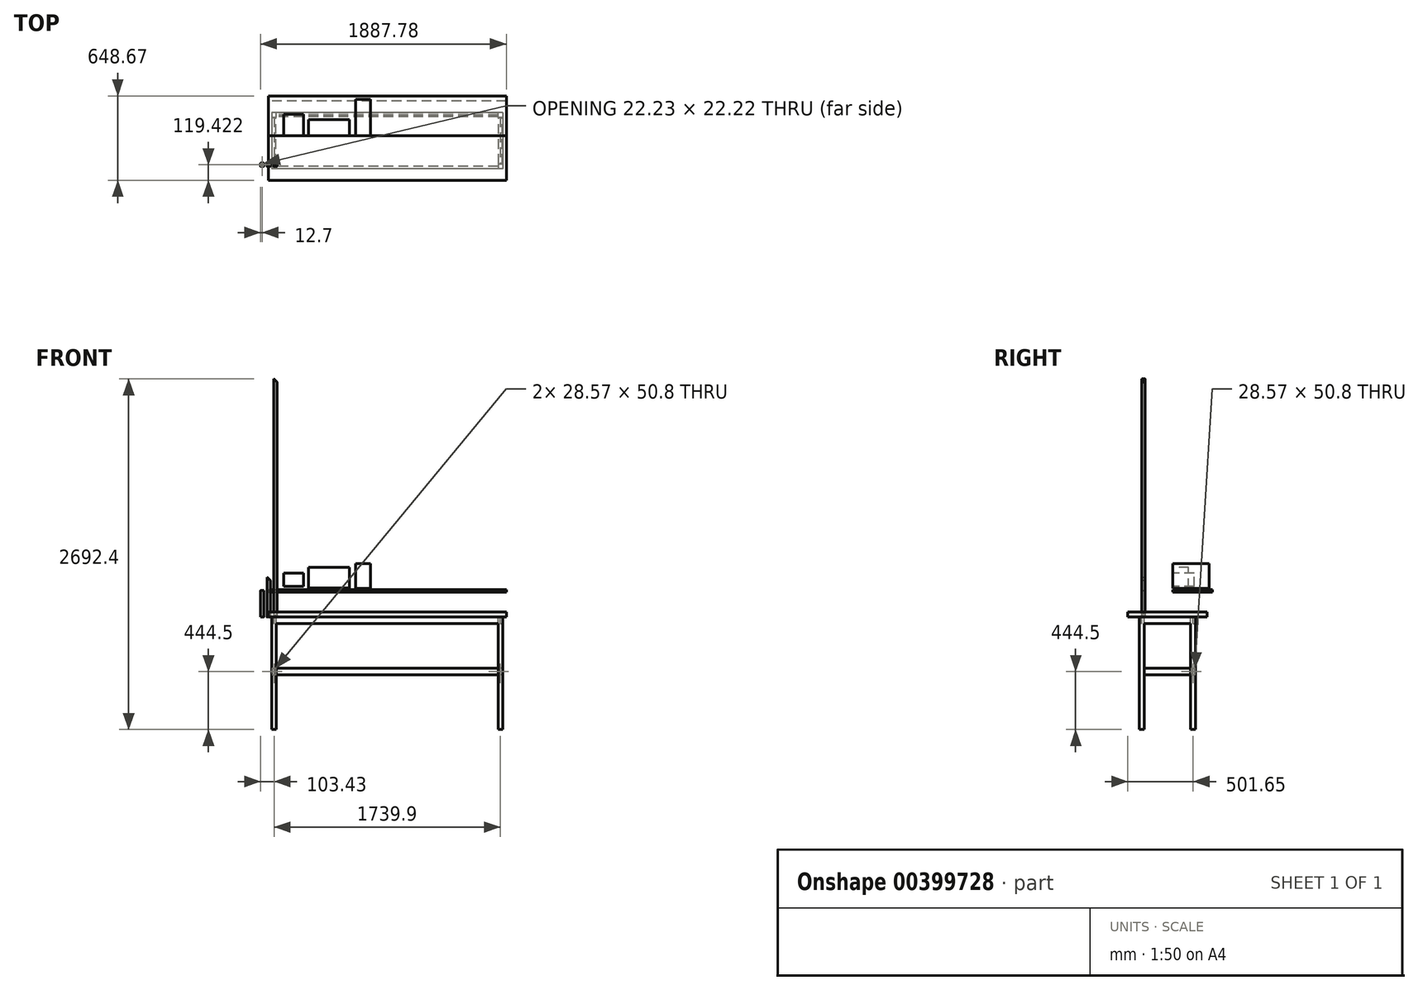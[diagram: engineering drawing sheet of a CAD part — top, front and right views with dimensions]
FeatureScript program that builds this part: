
annotation { "Feature Type Name" : "Feature", "Feature Type Description" : "" }
export const myFeature = defineFeature(function(context is Context, id is Id, definition is map)
    precondition{}
    {
        {
            var Q0;
            Q0=qCreatedBy(makeId("Top.planeOp"),FACE);
            var sketch = newSketch(context, id + "F0", { "sketchPlane" : qUnion([Q0])});
            skLineSegment(sketch, "E0.bottom", {"start": v(914.4, -304.8) * mm, "end": v(-914.4, -304.8) * mm});
            skLineSegment(sketch, "E0.top", {"start": v(914.4, 304.8) * mm, "end": v(-914.4, 304.8) * mm});
            skLineSegment(sketch, "E0.left", {"start": v(914.4, -304.8) * mm, "end": v(914.4, 304.8) * mm});
            skLineSegment(sketch, "E0.right", {"start": v(-914.4, -304.8) * mm, "end": v(-914.4, 304.8) * mm});
            skPoint(sketch, "E0.middle", {"position": v(0, 0) * mm});
            skSolve(sketch);
        }
        {
            var Q0;
            Q0=makeQuery(id+"F0.imprint","IMPRINT",FACE,{"disambiguationData":[TD([[makeQuery(id+"F0.imprint","IMPRINT",EDGE,{"derivedFrom":sQuery(id+"F0.wireOp",EDGE,"E0.bottom")}),-1.0]])]});
            extrude(context, id + "F1", {"entities" : qUnion([Q0]), "depth" : 38.1 * mm});
        }
        {
            var Q0;
            Q0=makeQuery(id+"F0.imprint","IMPRINT",FACE,{"disambiguationData":[TD([[makeQuery(id+"F0.imprint","IMPRINT",EDGE,{"derivedFrom":sQuery(id+"F0.wireOp",EDGE,"E0.bottom")}),-1.0]])]});
            var sketch = newSketch(context, id + "F2", { "sketchPlane" : qUnion([Q0])});
            skLineSegment(sketch, "E1.bottom", {"start": v(889, 215.9) * mm, "end": v(-889, 215.9) * mm});
            skLineSegment(sketch, "E1.top", {"start": v(889, -215.9) * mm, "end": v(-889, -215.9) * mm});
            skLineSegment(sketch, "E1.left", {"start": v(889, 215.9) * mm, "end": v(889, -215.9) * mm});
            skLineSegment(sketch, "E1.right", {"start": v(-889, 215.9) * mm, "end": v(-889, -215.9) * mm});
            skPoint(sketch, "E1.middle", {"position": v(0, 0) * mm});
            skLineSegment(sketch, "E2.bottom", {"start": v(850.9, 196.85) * mm, "end": v(-850.9, 196.85) * mm});
            skLineSegment(sketch, "E2.top", {"start": v(850.9, -196.85) * mm, "end": v(-850.9, -196.85) * mm});
            skLineSegment(sketch, "E2.left", {"start": v(869.95, 177.8) * mm, "end": v(869.95, -177.8) * mm});
            skLineSegment(sketch, "E2.right", {"start": v(-869.95, 177.8) * mm, "end": v(-869.95, -177.8) * mm});
            skLineSegment(sketch, "E3", {"start": v(0, -215.9) * mm, "end": v(0, 215.9) * mm, "construction": true});
            skPoint(sketch, "E4", {"position": v(-850.9, -177.8) * mm});
            skLineSegment(sketch, "E5", {"start": v(-889, 0) * mm, "end": v(0, 0) * mm, "construction": true});
            skLineSegment(sketch, "E6", {"start": v(-850.9, -177.8) * mm, "end": v(-889, -177.8) * mm});
            skLineSegment(sketch, "E7", {"start": v(-850.9, -177.8) * mm, "end": v(-850.9, -215.9) * mm});
            skLineSegment(sketch, "E8.MirrorCS", {"start": v(-850.9, 177.8) * mm, "end": v(-889, 177.8) * mm});
            skLineSegment(sketch, "E9.MirrorCS", {"start": v(-850.9, 177.8) * mm, "end": v(-850.9, 215.9) * mm});
            skLineSegment(sketch, "E10.MirrorCS", {"start": v(850.9, -177.8) * mm, "end": v(850.9, -215.9) * mm});
            skLineSegment(sketch, "E11.MirrorCS", {"start": v(850.9, -177.8) * mm, "end": v(889, -177.8) * mm});
            skLineSegment(sketch, "E12.MirrorCS", {"start": v(850.9, 177.8) * mm, "end": v(889, 177.8) * mm});
            skLineSegment(sketch, "E13.MirrorCS", {"start": v(850.9, 177.8) * mm, "end": v(850.9, 215.9) * mm});
            skPoint(sketch, "E14.orphan", {"position": v(869.95, -196.85) * mm});
            skPoint(sketch, "E15.orphan", {"position": v(869.95, 196.85) * mm});
            skPoint(sketch, "E16.orphan", {"position": v(-869.95, -196.85) * mm});
            skPoint(sketch, "E17.orphan", {"position": v(-869.95, 196.85) * mm});
            skSolve(sketch);
        }
        {
            var Q0;
            {var subQ0=sQuery(id+"F2.wireOp",EDGE,"E9.MirrorCS");var subQ1=sQuery(id+"F2.wireOp",EDGE,"E1.bottom");var subQ2=makeQuery(id+"F2.imprint","INTERSECT",VERTEX,{"derivedFrom":[subQ1,subQ0]});Q0=makeQuery(id+"F2.imprint","IMPRINT",FACE,{"disambiguationData":[TD([[makeQuery(id+"F2.imprint","IMPRINT",EDGE,{"disambiguationData":[TD([[subQ2,1.0]])],"derivedFrom":subQ1}),1.0]])]});}
            var Q1;
            {var subQ0=sQuery(id+"F2.wireOp",EDGE,"E7");var subQ1=sQuery(id+"F2.wireOp",EDGE,"E1.top");var subQ2=makeQuery(id+"F2.imprint","INTERSECT",VERTEX,{"derivedFrom":[subQ1,subQ0]});Q1=makeQuery(id+"F2.imprint","IMPRINT",FACE,{"disambiguationData":[TD([[makeQuery(id+"F2.imprint","IMPRINT",EDGE,{"disambiguationData":[TD([[subQ2,1.0]])],"derivedFrom":subQ1}),-1.0]])]});}
            var Q2;
            {var subQ0=sQuery(id+"F2.wireOp",EDGE,"E11.MirrorCS");var subQ1=sQuery(id+"F2.wireOp",EDGE,"E1.left");var subQ2=makeQuery(id+"F2.imprint","INTERSECT",VERTEX,{"derivedFrom":[subQ1,subQ0]});Q2=makeQuery(id+"F2.imprint","IMPRINT",FACE,{"disambiguationData":[TD([[makeQuery(id+"F2.imprint","IMPRINT",EDGE,{"disambiguationData":[TD([[subQ2,1.0]])],"derivedFrom":subQ1}),-1.0]])]});}
            var Q3;
            {var subQ0=sQuery(id+"F2.wireOp",EDGE,"E6");var subQ1=sQuery(id+"F2.wireOp",EDGE,"E1.right");var subQ2=makeQuery(id+"F2.imprint","INTERSECT",VERTEX,{"derivedFrom":[subQ1,subQ0]});Q3=makeQuery(id+"F2.imprint","IMPRINT",FACE,{"disambiguationData":[TD([[makeQuery(id+"F2.imprint","IMPRINT",EDGE,{"disambiguationData":[TD([[subQ2,1.0]])],"derivedFrom":subQ1}),1.0]])]});}
            extrude(context, id + "F3", {"entities" : qUnion([Q0, Q1, Q2, Q3]), "oppositeDirection" : true, "depth" : 50.8 * mm});
        }
        {
            var Q0;
            {var subQ2=sQuery(id+"F2.wireOp",EDGE,"E1.right");var subQ6=sQuery(id+"F2.wireOp",EDGE,"E1.top");var subQ7=makeQuery(id+"F2.imprint","INTERSECT",VERTEX,{"derivedFrom":[subQ6,subQ2]});Q0=makeQuery(id+"F2.imprint","IMPRINT",FACE,{"disambiguationData":[TD([[makeQuery(id+"F2.imprint","IMPRINT",EDGE,{"disambiguationData":[TD([[subQ7,1.0]])],"derivedFrom":subQ6}),-1.0]])]});}
            var Q1;
            {var subQ2=sQuery(id+"F2.wireOp",EDGE,"E1.right");var subQ6=sQuery(id+"F2.wireOp",EDGE,"E1.bottom");var subQ7=makeQuery(id+"F2.imprint","INTERSECT",VERTEX,{"derivedFrom":[subQ6,subQ2]});Q1=makeQuery(id+"F2.imprint","IMPRINT",FACE,{"disambiguationData":[TD([[makeQuery(id+"F2.imprint","IMPRINT",EDGE,{"disambiguationData":[TD([[subQ7,1.0]])],"derivedFrom":subQ6}),1.0]])]});}
            var Q2;
            {var subQ2=sQuery(id+"F2.wireOp",EDGE,"E1.top");var subQ4=sQuery(id+"F2.wireOp",EDGE,"E1.left");var subQ5=makeQuery(id+"F2.imprint","INTERSECT",VERTEX,{"derivedFrom":[subQ2,subQ4]});Q2=makeQuery(id+"F2.imprint","IMPRINT",FACE,{"disambiguationData":[TD([[makeQuery(id+"F2.imprint","IMPRINT",EDGE,{"disambiguationData":[TD([[subQ5,-1.0]])],"derivedFrom":subQ2}),-1.0]])]});}
            var Q3;
            {var subQ2=sQuery(id+"F2.wireOp",EDGE,"E1.left");var subQ6=sQuery(id+"F2.wireOp",EDGE,"E1.bottom");var subQ7=makeQuery(id+"F2.imprint","INTERSECT",VERTEX,{"derivedFrom":[subQ6,subQ2]});Q3=makeQuery(id+"F2.imprint","IMPRINT",FACE,{"disambiguationData":[TD([[makeQuery(id+"F2.imprint","IMPRINT",EDGE,{"disambiguationData":[TD([[subQ7,-1.0]])],"derivedFrom":subQ6}),1.0]])]});}
            extrude(context, id + "F4", {"entities" : qUnion([Q0, Q1, Q2, Q3]), "operationType" : NewBodyOperationType.ADD, "oppositeDirection" : true, "depth" : 863.6 * mm});
        }
        {
            var Q0;
            Q0=makeQuery(id+"F4.opExtrude","SWEPT_FACE",FACE,{"disambiguationData":[OSD([sQuery(id+"F2.wireOp",EDGE,"E9.MirrorCS")])]});
            var sketch = newSketch(context, id + "F5", { "sketchPlane" : qUnion([Q0])});
            skLineSegment(sketch, "E18", {"start": v(182.56, -393.7) * mm, "end": v(211.14, -393.7) * mm});
            skLineSegment(sketch, "E19", {"start": v(182.56, -444.5) * mm, "end": v(211.14, -444.5) * mm});
            skLineSegment(sketch, "E20", {"start": v(211.14, -393.7) * mm, "end": v(211.14, -444.5) * mm});
            skLineSegment(sketch, "E21", {"start": v(182.56, -393.7) * mm, "end": v(182.56, -444.5) * mm});
            skPoint(sketch, "E22", {"position": v(196.85, -393.7) * mm});
            skPoint(sketch, "E23", {"position": v(182.56, -419.1) * mm});
            skPoint(sketch, "E24", {"position": v(211.14, -419.1) * mm});
            skLineSegment(sketch, "E25", {"start": v(177.8, -385.16) * mm, "end": v(215.9, -385.16) * mm, "construction": true});
            skLineSegment(sketch, "E26", {"start": v(196.85, -385.16) * mm, "end": v(196.85, -459.18) * mm, "construction": true});
            skSolve(sketch);
        }
        {
            var Q0;
            Q0=makeQuery(id+"F5.imprint","IMPRINT",FACE,{"disambiguationData":[TD([[makeQuery(id+"F5.imprint","IMPRINT",EDGE,{"derivedFrom":sQuery(id+"F5.wireOp",EDGE,"E18")}),-1.0]])]});
            extrude(context, id + "F6", {"entities" : qUnion([Q0]), "operationType" : NewBodyOperationType.ADD, "endBound" : BoundingType.UP_TO_NEXT, "depth" : 25.4 * mm});
        }
        {
            var Q0;
            Q0=makeQuery(id+"F4.opExtrude","SWEPT_FACE",FACE,{"disambiguationData":[OSD([sQuery(id+"F2.wireOp",EDGE,"E8.MirrorCS")])]});
            var sketch = newSketch(context, id + "F7", { "sketchPlane" : qUnion([Q0])});
            skLineSegment(sketch, "E27", {"start": v(-884.24, -393.7) * mm, "end": v(-855.66, -393.7) * mm});
            skLineSegment(sketch, "E28", {"start": v(-884.24, -444.5) * mm, "end": v(-855.66, -444.5) * mm});
            skLineSegment(sketch, "E29", {"start": v(-855.66, -393.7) * mm, "end": v(-855.66, -444.5) * mm});
            skLineSegment(sketch, "E30", {"start": v(-884.24, -393.7) * mm, "end": v(-884.24, -444.5) * mm});
            skLineSegment(sketch, "E31", {"start": v(-889, -376.97) * mm, "end": v(-850.9, -376.97) * mm, "construction": true});
            skLineSegment(sketch, "E32", {"start": v(-869.95, -376.97) * mm, "end": v(-869.95, -445.4) * mm, "construction": true});
            skPoint(sketch, "E33", {"position": v(-884.24, -419.1) * mm});
            skPoint(sketch, "E34", {"position": v(-855.66, -419.1) * mm});
            skSolve(sketch);
        }
        {
            var Q0;
            Q0=makeQuery(id+"F7.imprint","IMPRINT",FACE,{"disambiguationData":[TD([[makeQuery(id+"F7.imprint","IMPRINT",EDGE,{"derivedFrom":sQuery(id+"F7.wireOp",EDGE,"E27")}),-1.0]])]});
            extrude(context, id + "F8", {"entities" : qUnion([Q0]), "endBound" : BoundingType.UP_TO_NEXT, "depth" : 25.4 * mm});
        }
        {
            var Q0;
            Q0=makeQuery(id+"F8.opExtrude","SWEPT_BODY",BODY,{"disambiguationData":[OSD([sQuery(id+"F7.wireOp",EDGE,"E27"),sQuery(id+"F7.wireOp",EDGE,"E28"),sQuery(id+"F7.wireOp",EDGE,"E29"),sQuery(id+"F7.wireOp",EDGE,"E30")])]});
            var Q1;
            Q1=qCreatedBy(makeId("Right.planeOp"),FACE);
            mirror(context, id + "F9", {"operationType" : NewBodyOperationType.ADD, "entities" : qUnion([Q0]), "mirrorPlane" : qUnion([Q1])});
        }
        {
            var Q0;
            Q0=makeQuery(id+"F1.opExtrude","CAP_FACE",FACE,{"disambiguationData":[OSD([sQuery(id+"F0.wireOp",EDGE,"E0.bottom"),sQuery(id+"F0.wireOp",EDGE,"E0.top"),sQuery(id+"F0.wireOp",EDGE,"E0.left"),sQuery(id+"F0.wireOp",EDGE,"E0.right")])],"isStart":false});
            cPlane(context, id + "F10", {"entities" : qUnion([Q0]), "cplaneType" : CPlaneType.OFFSET, "offset" : 152.4 * mm, "width" : 152.4 * mm, "height" : 152.4 * mm});
        }
        {
            var Q0;
            Q0=qCreatedBy(id+"F10.planeOp",FACE);
            var sketch = newSketch(context, id + "F11", { "sketchPlane" : qUnion([Q0])});
            skLineSegment(sketch, "E35.bottom", {"start": v(-914.4, 343.87) * mm, "end": v(914.4, 343.87) * mm});
            skLineSegment(sketch, "E35.top", {"start": v(-914.4, 39.07) * mm, "end": v(914.4, 39.07) * mm});
            skLineSegment(sketch, "E35.left", {"start": v(-914.4, 343.87) * mm, "end": v(-914.4, 39.07) * mm});
            skLineSegment(sketch, "E35.right", {"start": v(914.4, 343.87) * mm, "end": v(914.4, 39.07) * mm});
            skLineSegment(sketch, "E36", {"start": v(0, 343.87) * mm, "end": v(0, 39.07) * mm, "construction": true});
            skLineSegment(sketch, "E37", {"start": v(0, -304.8) * mm, "end": v(0, 304.8) * mm, "construction": true});
            skSolve(sketch);
        }
        {
            var Q0;
            Q0=makeQuery(id+"F11.imprint","IMPRINT",FACE,{"disambiguationData":[TD([[makeQuery(id+"F11.imprint","IMPRINT",EDGE,{"derivedFrom":sQuery(id+"F11.wireOp",EDGE,"E35.bottom")}),-1.0]])]});
            extrude(context, id + "F12", {"entities" : qUnion([Q0]), "depth" : 19.05 * mm});
        }
        {
            var Q0;
            Q0=makeQuery(id+"F12.opExtrude","SWEPT_FACE",FACE,{"disambiguationData":[OSD([sQuery(id+"F11.wireOp",EDGE,"E35.top")])]});
            var sketch = newSketch(context, id + "F13", { "sketchPlane" : qUnion([Q0])});
            skLineSegment(sketch, "E38.bottom", {"start": v(-796.5, 234.27) * mm, "end": v(-644.1, 234.27) * mm});
            skLineSegment(sketch, "E38.top", {"start": v(-796.5, 335.87) * mm, "end": v(-644.1, 335.87) * mm});
            skLineSegment(sketch, "E38.left", {"start": v(-796.5, 234.27) * mm, "end": v(-796.5, 335.87) * mm});
            skLineSegment(sketch, "E38.right", {"start": v(-644.1, 234.27) * mm, "end": v(-644.1, 335.87) * mm});
            skSolve(sketch);
        }
        {
            var Q0;
            Q0=makeQuery(id+"F13.imprint","IMPRINT",FACE,{"disambiguationData":[TD([[makeQuery(id+"F13.imprint","IMPRINT",EDGE,{"derivedFrom":sQuery(id+"F13.wireOp",EDGE,"E38.bottom")}),1.0]])]});
            extrude(context, id + "F14", {"entities" : qUnion([Q0]), "oppositeDirection" : true, "depth" : 165.1 * mm});
        }
        {
            var Q0;
            Q0=makeQuery(id+"F12.opExtrude","SWEPT_FACE",FACE,{"disambiguationData":[OSD([sQuery(id+"F11.wireOp",EDGE,"E35.top")])]});
            var sketch = newSketch(context, id + "F15", { "sketchPlane" : qUnion([Q0])});
            skLineSegment(sketch, "E39.bottom", {"start": v(-604.6, 221.37) * mm, "end": v(-291.5, 221.37) * mm});
            skLineSegment(sketch, "E39.top", {"start": v(-604.6, 382.17) * mm, "end": v(-291.5, 382.17) * mm});
            skLineSegment(sketch, "E39.left", {"start": v(-604.6, 221.37) * mm, "end": v(-604.6, 382.17) * mm});
            skLineSegment(sketch, "E39.right", {"start": v(-291.5, 221.37) * mm, "end": v(-291.5, 382.17) * mm});
            skSolve(sketch);
        }
        {
            var Q0;
            Q0=makeQuery(id+"F15.imprint","IMPRINT",FACE,{"disambiguationData":[TD([[makeQuery(id+"F15.imprint","IMPRINT",EDGE,{"derivedFrom":sQuery(id+"F15.wireOp",EDGE,"E39.bottom")}),1.0]])]});
            extrude(context, id + "F16", {"entities" : qUnion([Q0]), "oppositeDirection" : true, "depth" : 122.4 * mm});
        }
        {
            var Q0;
            Q0=makeQuery(id+"F12.opExtrude","SWEPT_FACE",FACE,{"disambiguationData":[OSD([sQuery(id+"F11.wireOp",EDGE,"E35.top")])]});
            var sketch = newSketch(context, id + "F17", { "sketchPlane" : qUnion([Q0])});
            skLineSegment(sketch, "E40.bottom", {"start": v(-243.83, 409.85) * mm, "end": v(-129.53, 409.85) * mm});
            skLineSegment(sketch, "E40.top", {"start": v(-243.83, 219.35) * mm, "end": v(-129.53, 219.35) * mm});
            skLineSegment(sketch, "E40.left", {"start": v(-243.83, 409.85) * mm, "end": v(-243.83, 219.35) * mm});
            skLineSegment(sketch, "E40.right", {"start": v(-129.53, 409.85) * mm, "end": v(-129.53, 219.35) * mm});
            skSolve(sketch);
        }
        {
            var Q0;
            Q0=makeQuery(id+"F17.imprint","IMPRINT",FACE,{"disambiguationData":[TD([[makeQuery(id+"F17.imprint","IMPRINT",EDGE,{"derivedFrom":sQuery(id+"F17.wireOp",EDGE,"E40.bottom")}),-1.0]])]});
            extrude(context, id + "F18", {"entities" : qUnion([Q0]), "oppositeDirection" : true, "depth" : 279.4 * mm});
        }
        {
            var Q0;
            Q0=makeQuery(id+"F12.opExtrude","CAP_FACE",FACE,{"disambiguationData":[OSD([sQuery(id+"F11.wireOp",EDGE,"E35.bottom"),sQuery(id+"F11.wireOp",EDGE,"E35.top"),sQuery(id+"F11.wireOp",EDGE,"E35.left"),sQuery(id+"F11.wireOp",EDGE,"E35.right")])],"isStart":true});
            var sketch = newSketch(context, id + "F19", { "sketchPlane" : qUnion([Q0])});
            skLineSegment(sketch, "E41.0", {"start": v(-914.4, -39.07) * mm, "end": v(914.4, -39.07) * mm});
            skLineSegment(sketch, "E42.0", {"start": v(-914.4, -343.87) * mm, "end": v(-914.4, -39.07) * mm});
            skLineSegment(sketch, "E43.0", {"start": v(-914.4, -343.87) * mm, "end": v(914.4, -343.87) * mm});
            skLineSegment(sketch, "E44.0", {"start": v(914.4, -343.87) * mm, "end": v(914.4, -39.07) * mm});
            skLineSegment(sketch, "E45", {"start": v(-914.4, -64.47) * mm, "end": v(914.4, -64.47) * mm});
            skLineSegment(sketch, "E46", {"start": v(-914.4, -318.47) * mm, "end": v(914.4, -318.47) * mm});
            skLineSegment(sketch, "E47", {"start": v(-889, -64.47) * mm, "end": v(-889, -318.47) * mm});
            skLineSegment(sketch, "E48", {"start": v(889, -64.47) * mm, "end": v(889, -318.47) * mm});
            skSolve(sketch);
        }
        {
            var Q0;
            Q0=qCreatedBy(makeId("Top.planeOp"),FACE);
            var sketch = newSketch(context, id + "F20", { "sketchPlane" : qUnion([Q0])});
            skLineSegment(sketch, "E49.bottom", {"start": v(-871.14, -198.08) * mm, "end": v(-847.01, -198.08) * mm});
            skLineSegment(sketch, "E49.top", {"start": v(-871.14, -172.68) * mm, "end": v(-847.01, -172.68) * mm});
            skLineSegment(sketch, "E49.left", {"start": v(-871.78, -197.44) * mm, "end": v(-871.78, -173.31) * mm});
            skLineSegment(sketch, "E49.right", {"start": v(-846.38, -197.44) * mm, "end": v(-846.38, -173.31) * mm});
            skLineSegment(sketch, "E50.0", {"start": v(-869.56, -196.5) * mm, "end": v(-848.6, -196.5) * mm});
            skLineSegment(sketch, "E50.1", {"start": v(-870.2, -195.86) * mm, "end": v(-870.2, -174.9) * mm});
            skLineSegment(sketch, "E50.2", {"start": v(-869.56, -174.27) * mm, "end": v(-848.6, -174.27) * mm});
            skLineSegment(sketch, "E50.3", {"start": v(-847.97, -195.86) * mm, "end": v(-847.97, -174.9) * mm});
            skPoint(sketch, "E51.visualSharp", {"position": v(-846.38, -198.08) * mm});
            skArc(sketch, "E51.filletArc", {"start": v(-847.01, -198.08) * mm, "mid": v(-846.57, -197.9) * mm, "end": v(-846.38, -197.44) * mm});
            skPoint(sketch, "E52.visualSharp", {"position": v(-846.38, -172.68) * mm});
            skArc(sketch, "E52.filletArc", {"start": v(-846.38, -173.31) * mm, "mid": v(-846.57, -172.86) * mm, "end": v(-847.01, -172.68) * mm});
            skPoint(sketch, "E53.visualSharp", {"position": v(-871.78, -172.68) * mm});
            skArc(sketch, "E53.filletArc", {"start": v(-871.14, -172.68) * mm, "mid": v(-871.6, -172.86) * mm, "end": v(-871.78, -173.31) * mm});
            skPoint(sketch, "E54.visualSharp", {"position": v(-871.78, -198.08) * mm});
            skArc(sketch, "E54.filletArc", {"start": v(-871.78, -197.44) * mm, "mid": v(-871.6, -197.9) * mm, "end": v(-871.14, -198.08) * mm});
            skPoint(sketch, "E55.visualSharp", {"position": v(-847.97, -196.5) * mm});
            skArc(sketch, "E55.filletArc", {"start": v(-848.6, -196.5) * mm, "mid": v(-848.15, -196.3) * mm, "end": v(-847.97, -195.86) * mm});
            skPoint(sketch, "E56.visualSharp", {"position": v(-847.97, -174.27) * mm});
            skArc(sketch, "E56.filletArc", {"start": v(-847.97, -174.9) * mm, "mid": v(-848.15, -174.45) * mm, "end": v(-848.6, -174.27) * mm});
            skPoint(sketch, "E57.visualSharp", {"position": v(-870.2, -174.27) * mm});
            skArc(sketch, "E57.filletArc", {"start": v(-869.56, -174.27) * mm, "mid": v(-870, -174.45) * mm, "end": v(-870.2, -174.9) * mm});
            skPoint(sketch, "E58.visualSharp", {"position": v(-870.2, -196.5) * mm});
            skArc(sketch, "E58.filletArc", {"start": v(-870.2, -195.86) * mm, "mid": v(-870, -196.3) * mm, "end": v(-869.56, -196.5) * mm});
            skLineSegment(sketch, "E59.1.0.0", {"start": v(-921.94, -198.08) * mm, "end": v(-897.81, -198.08) * mm});
            skArc(sketch, "E59.1.0.1", {"start": v(-922.58, -197.44) * mm, "mid": v(-922.4, -197.9) * mm, "end": v(-921.94, -198.08) * mm});
            skLineSegment(sketch, "E59.1.0.2", {"start": v(-922.58, -197.44) * mm, "end": v(-922.58, -173.31) * mm});
            skArc(sketch, "E59.1.0.3", {"start": v(-921.94, -172.68) * mm, "mid": v(-922.4, -172.86) * mm, "end": v(-922.58, -173.31) * mm});
            skLineSegment(sketch, "E59.1.0.4", {"start": v(-921.94, -172.68) * mm, "end": v(-897.81, -172.68) * mm});
            skArc(sketch, "E59.1.0.5", {"start": v(-897.18, -173.31) * mm, "mid": v(-897.37, -172.86) * mm, "end": v(-897.81, -172.68) * mm});
            skLineSegment(sketch, "E59.1.0.6", {"start": v(-897.18, -197.44) * mm, "end": v(-897.18, -173.31) * mm});
            skArc(sketch, "E59.1.0.7", {"start": v(-897.81, -198.08) * mm, "mid": v(-897.37, -197.9) * mm, "end": v(-897.18, -197.44) * mm});
            skArc(sketch, "E59.1.0.8", {"start": v(-899.4, -196.5) * mm, "mid": v(-898.95, -196.3) * mm, "end": v(-898.77, -195.86) * mm});
            skLineSegment(sketch, "E59.1.0.9", {"start": v(-898.77, -195.86) * mm, "end": v(-898.77, -174.9) * mm});
            skArc(sketch, "E59.1.0.10", {"start": v(-898.77, -174.9) * mm, "mid": v(-898.95, -174.45) * mm, "end": v(-899.4, -174.27) * mm});
            skLineSegment(sketch, "E59.1.0.11", {"start": v(-920.36, -174.27) * mm, "end": v(-899.4, -174.27) * mm});
            skArc(sketch, "E59.1.0.12", {"start": v(-920.36, -174.27) * mm, "mid": v(-920.8, -174.45) * mm, "end": v(-921, -174.9) * mm});
            skLineSegment(sketch, "E59.1.0.13", {"start": v(-921, -195.86) * mm, "end": v(-921, -174.9) * mm});
            skArc(sketch, "E59.1.0.14", {"start": v(-921, -195.86) * mm, "mid": v(-920.8, -196.3) * mm, "end": v(-920.36, -196.5) * mm});
            skLineSegment(sketch, "E59.1.0.15", {"start": v(-920.36, -196.5) * mm, "end": v(-899.4, -196.5) * mm});
            skLineSegment(sketch, "E59.2.0.0", {"start": v(-972.74, -198.08) * mm, "end": v(-948.61, -198.08) * mm});
            skArc(sketch, "E59.2.0.1", {"start": v(-973.38, -197.44) * mm, "mid": v(-973.2, -197.9) * mm, "end": v(-972.74, -198.08) * mm});
            skLineSegment(sketch, "E59.2.0.2", {"start": v(-973.38, -197.44) * mm, "end": v(-973.38, -173.31) * mm});
            skArc(sketch, "E59.2.0.3", {"start": v(-972.74, -172.68) * mm, "mid": v(-973.2, -172.86) * mm, "end": v(-973.38, -173.31) * mm});
            skLineSegment(sketch, "E59.2.0.4", {"start": v(-972.74, -172.68) * mm, "end": v(-948.61, -172.68) * mm});
            skArc(sketch, "E59.2.0.5", {"start": v(-947.98, -173.31) * mm, "mid": v(-948.17, -172.86) * mm, "end": v(-948.61, -172.68) * mm});
            skLineSegment(sketch, "E59.2.0.6", {"start": v(-947.98, -197.44) * mm, "end": v(-947.98, -173.31) * mm});
            skArc(sketch, "E59.2.0.7", {"start": v(-948.61, -198.08) * mm, "mid": v(-948.17, -197.9) * mm, "end": v(-947.98, -197.44) * mm});
            skArc(sketch, "E59.2.0.8", {"start": v(-950.2, -196.5) * mm, "mid": v(-949.75, -196.3) * mm, "end": v(-949.57, -195.86) * mm});
            skLineSegment(sketch, "E59.2.0.9", {"start": v(-949.57, -195.86) * mm, "end": v(-949.57, -174.9) * mm});
            skArc(sketch, "E59.2.0.10", {"start": v(-949.57, -174.9) * mm, "mid": v(-949.75, -174.45) * mm, "end": v(-950.2, -174.27) * mm});
            skLineSegment(sketch, "E59.2.0.11", {"start": v(-971.16, -174.27) * mm, "end": v(-950.2, -174.27) * mm});
            skArc(sketch, "E59.2.0.12", {"start": v(-971.16, -174.27) * mm, "mid": v(-971.6, -174.45) * mm, "end": v(-971.8, -174.9) * mm});
            skLineSegment(sketch, "E59.2.0.13", {"start": v(-971.8, -195.86) * mm, "end": v(-971.8, -174.9) * mm});
            skArc(sketch, "E59.2.0.14", {"start": v(-971.8, -195.86) * mm, "mid": v(-971.6, -196.3) * mm, "end": v(-971.16, -196.5) * mm});
            skLineSegment(sketch, "E59.2.0.15", {"start": v(-971.16, -196.5) * mm, "end": v(-950.2, -196.5) * mm});
            skLineSegment(sketch, "E59.direction1", {"start": v(-921.94, -198.08) * mm, "end": v(-871.14, -198.08) * mm, "construction": true});
            skSolve(sketch);
        }
        {
            var Q0;
            Q0=makeQuery(id+"F20.imprint","IMPRINT",FACE,{"disambiguationData":[TD([[makeQuery(id+"F20.imprint","IMPRINT",EDGE,{"derivedFrom":sQuery(id+"F20.wireOp",EDGE,"E49.bottom")}),1.0]])]});
            extrude(context, id + "F21", {"entities" : qUnion([Q0]), "depth" : 1828.8 * mm});
        }
        {
            var Q0;
            Q0=makeQuery(id+"F20.imprint","IMPRINT",FACE,{"disambiguationData":[TD([[makeQuery(id+"F20.imprint","IMPRINT",EDGE,{"derivedFrom":sQuery(id+"F20.wireOp",EDGE,"E59.1.0.0")}),1.0]])]});
            extrude(context, id + "F22", {"entities" : qUnion([Q0]), "depth" : 304.8 * mm});
        }
        {
            var Q0;
            Q0=makeQuery(id+"F20.imprint","IMPRINT",FACE,{"disambiguationData":[TD([[makeQuery(id+"F20.imprint","IMPRINT",EDGE,{"derivedFrom":sQuery(id+"F20.wireOp",EDGE,"E59.2.0.0")}),1.0]])]});
            extrude(context, id + "F23", {"entities" : qUnion([Q0]), "depth" : 203.2 * mm});
        }
        {
            var Q0;
            Q0=makeQuery(id+"F22.opExtrude","SWEPT_FACE",FACE,{"disambiguationData":[OSD([sQuery(id+"F20.wireOp",EDGE,"E59.1.0.0")])]});
            var sketch = newSketch(context, id + "F24", { "sketchPlane" : qUnion([Q0])});
            skLineSegment(sketch, "E60.0", {"start": v(-897.18, 25.4) * mm, "end": v(-897.18, 0) * mm});
            skLineSegment(sketch, "E61", {"start": v(-922.58, 0) * mm, "end": v(-897.18, 25.4) * mm});
            skPoint(sketch, "E62.0.start.orphan", {"position": v(-922.58, 304.8) * mm});
            skPoint(sketch, "E63.orphan", {"position": v(-897.18, 304.8) * mm});
            skLineSegment(sketch, "E64", {"start": v(-922.58, 0) * mm, "end": v(-897.18, 0) * mm});
            skLineSegment(sketch, "E65", {"start": v(-921.94, 152.4) * mm, "end": v(-897.81, 152.4) * mm, "construction": true});
            skLineSegment(sketch, "E66.MirrorCS", {"start": v(-922.58, 304.8) * mm, "end": v(-897.18, 279.4) * mm});
            skLineSegment(sketch, "E67.MirrorCS", {"start": v(-897.18, 279.4) * mm, "end": v(-897.18, 304.8) * mm});
            skLineSegment(sketch, "E68.MirrorCS", {"start": v(-922.58, 304.8) * mm, "end": v(-897.18, 304.8) * mm});
            skSolve(sketch);
        }
        {
            var Q0;
            Q0=makeQuery(id+"F21.opExtrude","SWEPT_FACE",FACE,{"disambiguationData":[OSD([sQuery(id+"F20.wireOp",EDGE,"E49.bottom")])]});
            var sketch = newSketch(context, id + "F25", { "sketchPlane" : qUnion([Q0])});
            skLineSegment(sketch, "E69.0", {"start": v(-871.78, 0) * mm, "end": v(-846.38, 0) * mm});
            skLineSegment(sketch, "E70.0", {"start": v(-846.38, 25.4) * mm, "end": v(-846.38, 0) * mm});
            skLineSegment(sketch, "E71", {"start": v(-871.78, 0) * mm, "end": v(-846.38, 25.4) * mm});
            skPoint(sketch, "E72.orphan", {"position": v(-846.38, 1828.8) * mm});
            skPoint(sketch, "E73.orphan", {"position": v(-871.14, 0) * mm});
            skLineSegment(sketch, "E74", {"start": v(-871.14, 914.4) * mm, "end": v(-847.01, 914.4) * mm, "construction": true});
            skLineSegment(sketch, "E75.MirrorCS", {"start": v(-871.78, 1828.8) * mm, "end": v(-846.38, 1803.4) * mm});
            skLineSegment(sketch, "E76.MirrorCS", {"start": v(-846.38, 1803.4) * mm, "end": v(-846.38, 1828.8) * mm});
            skLineSegment(sketch, "E77.MirrorCS", {"start": v(-871.78, 1828.8) * mm, "end": v(-846.38, 1828.8) * mm});
            skSolve(sketch);
        }
        {
            var Q0;
            {var subQ0=sQuery(id+"F25.wireOp",EDGE,"E76.MirrorCS");Q0=makeQuery(id+"F25.imprint","IMPRINT",FACE,{"disambiguationData":[TD([[makeQuery(id+"F25.imprint","IMPRINT",EDGE,{"derivedFrom":subQ0}),1.0]])]});}
            var Q1;
            {var subQ0=sQuery(id+"F25.wireOp",EDGE,"E75.MirrorCS");var subQ1=sQuery(id+"F20.wireOp",EDGE,"E49.bottom");var subQ2=makeQuery(id+"F21.opExtrude","SWEPT_EDGE",EDGE,{"disambiguationData":[OSD([subQ1,sQuery(id+"F20.wireOp",EDGE,"E54.filletArc")])]});var subQ3=makeQuery(id+"F25.imprint","INTERSECT",VERTEX,{"derivedFrom":[subQ2,subQ0]});Q1=makeQuery(id+"F25.imprint","IMPRINT",FACE,{"disambiguationData":[TD([[makeQuery(id+"F25.imprint","IMPRINT",EDGE,{"disambiguationData":[TD([[subQ3,-1.0]])],"derivedFrom":subQ0}),1.0]])]});}
            var Q2;
            {var subQ0=sQuery(id+"F25.wireOp",EDGE,"E77.MirrorCS");var subQ1=sQuery(id+"F25.wireOp",EDGE,"E75.MirrorCS");var subQ2=makeQuery(id+"F25.imprint","INTERSECT",VERTEX,{"derivedFrom":[subQ1,subQ0]});Q2=makeQuery(id+"F25.imprint","IMPRINT",FACE,{"disambiguationData":[TD([[makeQuery(id+"F25.imprint","IMPRINT",EDGE,{"disambiguationData":[TD([[subQ2,-1.0]])],"derivedFrom":subQ1}),1.0]])]});}
            var Q3;
            {var subQ0=sQuery(id+"F25.wireOp",EDGE,"E69.0");var subQ1=sQuery(id+"F20.wireOp",EDGE,"E49.bottom");var subQ2=makeQuery(id+"F21.opExtrude","SWEPT_EDGE",EDGE,{"disambiguationData":[OSD([subQ1,sQuery(id+"F20.wireOp",EDGE,"E54.filletArc")])]});var subQ3=makeQuery(id+"F25.imprint","INTERSECT",VERTEX,{"derivedFrom":[subQ2,subQ0]});Q3=makeQuery(id+"F25.imprint","IMPRINT",FACE,{"disambiguationData":[TD([[makeQuery(id+"F25.imprint","IMPRINT",EDGE,{"disambiguationData":[TD([[subQ3,-1.0]])],"derivedFrom":subQ0}),1.0]])]});}
            var Q4;
            {var subQ3=sQuery(id+"F25.wireOp",EDGE,"E70.0");Q4=makeQuery(id+"F25.imprint","IMPRINT",FACE,{"disambiguationData":[TD([[makeQuery(id+"F25.imprint","IMPRINT",EDGE,{"derivedFrom":subQ3}),-1.0]])]});}
            var Q5;
            {var subQ0=sQuery(id+"F25.wireOp",EDGE,"E69.0");var subQ3=sQuery(id+"F25.wireOp",EDGE,"E71");var subQ4=makeQuery(id+"F25.imprint","INTERSECT",VERTEX,{"derivedFrom":[subQ0,subQ3]});Q5=makeQuery(id+"F25.imprint","IMPRINT",FACE,{"disambiguationData":[TD([[makeQuery(id+"F25.imprint","IMPRINT",EDGE,{"disambiguationData":[TD([[subQ4,-1.0]])],"derivedFrom":subQ0}),1.0]])]});}
            var Q6;
            {var subQ0=sQuery(id+"F24.wireOp",EDGE,"E60.0");Q6=makeQuery(id+"F24.imprint","IMPRINT",FACE,{"disambiguationData":[TD([[makeQuery(id+"F24.imprint","IMPRINT",EDGE,{"derivedFrom":subQ0}),-1.0]])]});}
            var Q7;
            {var subQ0=sQuery(id+"F24.wireOp",EDGE,"E61");var subQ1=sQuery(id+"F20.wireOp",EDGE,"E59.1.0.0");var subQ2=makeQuery(id+"F22.opExtrude","SWEPT_EDGE",EDGE,{"disambiguationData":[OSD([subQ1,sQuery(id+"F20.wireOp",EDGE,"E59.1.0.1")])]});var subQ3=makeQuery(id+"F24.imprint","INTERSECT",VERTEX,{"derivedFrom":[subQ2,subQ0]});Q7=makeQuery(id+"F24.imprint","IMPRINT",FACE,{"disambiguationData":[TD([[makeQuery(id+"F24.imprint","IMPRINT",EDGE,{"disambiguationData":[TD([[subQ3,-1.0]])],"derivedFrom":subQ0}),-1.0]])]});}
            var Q8;
            {var subQ0=sQuery(id+"F24.wireOp",EDGE,"E64");var subQ1=sQuery(id+"F24.wireOp",EDGE,"E61");var subQ2=makeQuery(id+"F24.imprint","INTERSECT",VERTEX,{"derivedFrom":[subQ1,subQ0]});Q8=makeQuery(id+"F24.imprint","IMPRINT",FACE,{"disambiguationData":[TD([[makeQuery(id+"F24.imprint","IMPRINT",EDGE,{"disambiguationData":[TD([[subQ2,-1.0]])],"derivedFrom":subQ1}),-1.0]])]});}
            var Q9;
            {var subQ0=sQuery(id+"F24.wireOp",EDGE,"E67.MirrorCS");Q9=makeQuery(id+"F24.imprint","IMPRINT",FACE,{"disambiguationData":[TD([[makeQuery(id+"F24.imprint","IMPRINT",EDGE,{"derivedFrom":subQ0}),1.0]])]});}
            var Q10;
            {var subQ0=sQuery(id+"F24.wireOp",EDGE,"E66.MirrorCS");var subQ1=sQuery(id+"F20.wireOp",EDGE,"E59.1.0.0");var subQ2=makeQuery(id+"F22.opExtrude","SWEPT_EDGE",EDGE,{"disambiguationData":[OSD([subQ1,sQuery(id+"F20.wireOp",EDGE,"E59.1.0.1")])]});var subQ3=makeQuery(id+"F24.imprint","INTERSECT",VERTEX,{"derivedFrom":[subQ2,subQ0]});Q10=makeQuery(id+"F24.imprint","IMPRINT",FACE,{"disambiguationData":[TD([[makeQuery(id+"F24.imprint","IMPRINT",EDGE,{"disambiguationData":[TD([[subQ3,-1.0]])],"derivedFrom":subQ0}),1.0]])]});}
            var Q11;
            {var subQ0=sQuery(id+"F24.wireOp",EDGE,"E68.MirrorCS");var subQ1=sQuery(id+"F24.wireOp",EDGE,"E66.MirrorCS");var subQ2=makeQuery(id+"F24.imprint","INTERSECT",VERTEX,{"derivedFrom":[subQ1,subQ0]});Q11=makeQuery(id+"F24.imprint","IMPRINT",FACE,{"disambiguationData":[TD([[makeQuery(id+"F24.imprint","IMPRINT",EDGE,{"disambiguationData":[TD([[subQ2,-1.0]])],"derivedFrom":subQ1}),1.0]])]});}
            extrude(context, id + "F26", {"entities" : qUnion([Q0, Q1, Q2, Q3, Q4, Q5, Q6, Q7, Q8, Q9, Q10, Q11]), "operationType" : NewBodyOperationType.REMOVE, "oppositeDirection" : true, "depth" : 25.4 * mm});
        }
    });
